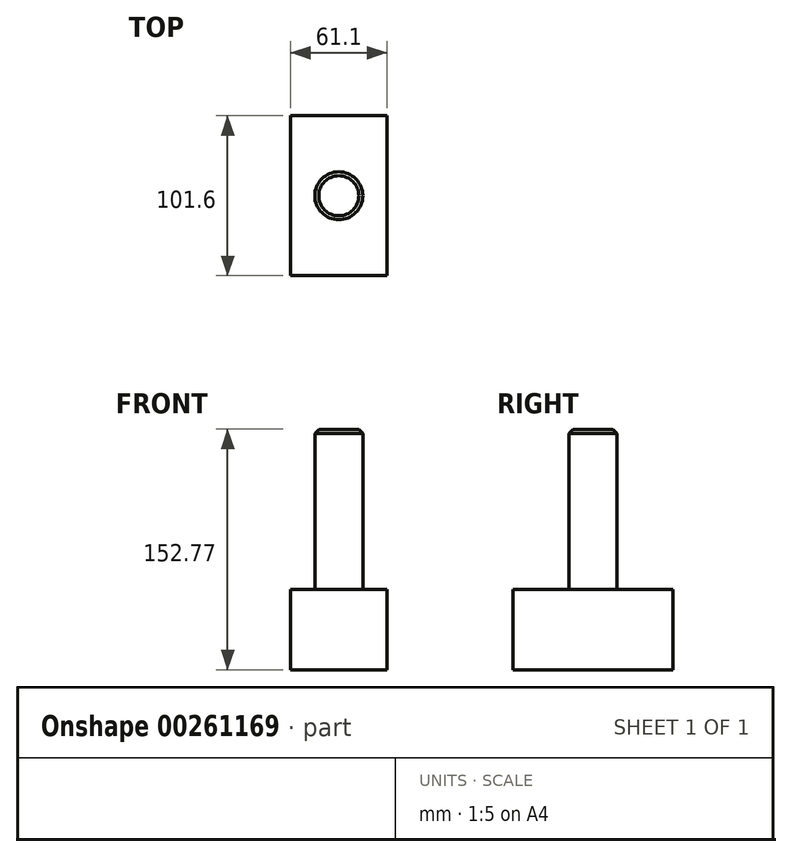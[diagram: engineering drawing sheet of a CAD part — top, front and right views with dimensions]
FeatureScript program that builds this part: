
annotation { "Feature Type Name" : "Feature", "Feature Type Description" : "" }
export const myFeature = defineFeature(function(context is Context, id is Id, definition is map)
    precondition{}
    {
        {
            var Q0;
            Q0=qCreatedBy(makeId("Front.planeOp"),FACE);
            var sketch = newSketch(context, id + "F0", { "sketchPlane" : qUnion([Q0])});
            skLineSegment(sketch, "E0", {"start": v(0, 29.47) * mm, "end": v(-33.6, 29.47) * mm});
            skLineSegment(sketch, "E1", {"start": v(-33.6, 29.47) * mm, "end": v(-33.6, -21.7) * mm});
            skLineSegment(sketch, "E2", {"start": v(-33.6, -21.7) * mm, "end": v(27.5, -21.7) * mm});
            skLineSegment(sketch, "E3", {"start": v(27.5, -21.7) * mm, "end": v(27.5, 29.47) * mm});
            skLineSegment(sketch, "E4", {"start": v(27.5, 29.47) * mm, "end": v(0, 29.47) * mm});
            skSolve(sketch);
        }
        {
            var Q0;
            Q0 = qSketchRegion(id + "F0", true);
            extrude(context, id + "F1", {"entities" : qUnion([Q0]), "depth" : 101.6 * mm});
        }
        {
            var Q0;
            Q0=makeQuery(id+"F1.opExtrude","SWEPT_FACE",FACE,{"disambiguationData":[OSD([sQuery(id+"F0.wireOp",EDGE,"E0"),sQuery(id+"F0.wireOp",EDGE,"E4")])]});
            var sketch = newSketch(context, id + "F2", { "sketchPlane" : qUnion([Q0])});
            skCircle(sketch, "E5", {"center": v(-3.06, -50.8) * mm, "radius": 15.24 * mm});
            skPoint(sketch, "E5.centerSnap0", {"position": v(27.5, -50.8) * mm});
            skPoint(sketch, "E5.centerSnap1", {"position": v(-3.06, -101.6) * mm});
            skSolve(sketch);
        }
        {
            var Q0;
            Q0 = qSketchRegion(id + "F2", true);
            extrude(context, id + "F3", {"entities" : qUnion([Q0]), "operationType" : NewBodyOperationType.ADD, "depth" : 101.6 * mm});
        }
        {
            var Q0;
            Q0=makeQuery(id+"F3.opExtrude","CAP_FACE",FACE,{"disambiguationData":[OSD([sQuery(id+"F2.wireOp",EDGE,"E5")])],"isStart":false});
            chamfer(context, id + "F4", {"entities" : qUnion([Q0]), "width" : 2.54 * mm, "tangentPropagation" : true});
        }
    });
